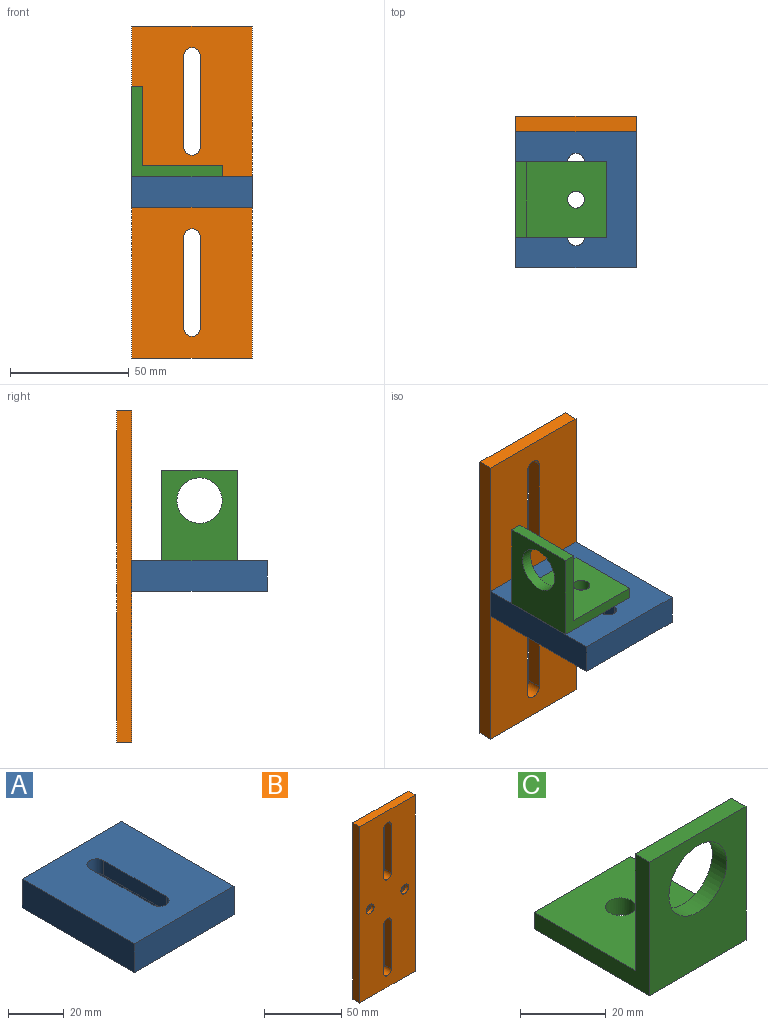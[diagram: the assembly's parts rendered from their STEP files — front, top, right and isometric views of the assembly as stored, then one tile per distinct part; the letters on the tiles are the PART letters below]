
ASSEMBLY  parts=3 mates=2
PART A: 19 faces, bbox 50.8x57.2x12.7 mm
  f0: cylinder r=3.57mm len=7.14mm, axis (0,0,-1), area 71.2mm2, adj f1,f7,f8,f14
  f1: plane 31.75x6.35mm, normal (-1,0,0), area 201.6mm2, adj f0,f2,f8,f14
  f2: cylinder r=3.57mm len=7.14mm, axis (0,0,-1), area 71.2mm2, adj f1,f7,f8,f14
  f3: plane 50.8x12.7mm, normal (0,1,0), area 604.2mm2, adj f4,f6,f8,f9,f16,f18
  f4: plane 57.15x12.7mm, normal (-1,0,0), area 725.8mm2, adj f3,f5,f8,f9
  f5: plane 50.8x12.7mm, normal (0,-1,0), area 645.2mm2, adj f4,f6,f8,f9
  f6: plane 57.15x12.7mm, normal (1,0,0), area 725.8mm2, adj f3,f5,f8,f9
  f7: plane 31.75x6.35mm, normal (1,0,0), area 201.6mm2, adj f0,f2,f8,f14
  f8: plane 57.15x50.8mm, normal (0,0,1), area 2636.6mm2, adj f0,f1,f2,f3,f4,f5,f6,f7
  f9: plane 57.15x50.8mm, normal (0,0,-1), area 2452.8mm2, adj f3,f4,f5,f6,f10,f11,f12,f13
  f10: plane 31.75x6.35mm, normal (1,0,0), area 201.6mm2, adj f9,f11,f13,f14
  f11: cylinder r=5.56mm len=11.13mm, axis (0,0,-1), area 111mm2, adj f9,f10,f12,f14
  f12: plane 31.75x6.35mm, normal (-1,0,0), area 201.6mm2, adj f9,f11,f13,f14
  f13: cylinder r=5.56mm len=11.13mm, axis (0,0,-1), area 111mm2, adj f9,f10,f12,f14
  f14: plane 42.88x11.13mm, normal (0,0,-1), area 183.8mm2, adj f0,f1,f2,f7,f10,f11,f12,f13
  f15: cone r=0mm half-angle=59deg, axis (0,1,0), area 23.9mm2, adj f16
  f16: cylinder r=2.55mm len=25.4mm, axis (0,1,0), area 407.4mm2, adj f3,f15
  f17: cone r=0mm half-angle=59deg, axis (0,1,0), area 23.9mm2, adj f18
  f18: cylinder r=2.55mm len=25.4mm, axis (0,1,0), area 407.4mm2, adj f3,f17
PART B: 18 faces, bbox 50.8x6.4x139.7 mm
  f0: plane 50.8x6.35mm, normal (0,0,1), area 322.6mm2, adj f1,f11,f12,f13
  f1: plane 139.7x6.35mm, normal (-1,0,0), area 887.1mm2, adj f0,f2,f12,f13
  f2: plane 50.8x6.35mm, normal (0,0,-1), area 322.6mm2, adj f1,f11,f12,f13
  f3: cylinder r=3.57mm len=7.14mm, axis (0,1,0), area 71.2mm2, adj f4,f9,f12,f13
  f4: plane 38.1x6.35mm, normal (-1,0,0), area 241.9mm2, adj f3,f5,f12,f13
  f5: cylinder r=3.57mm len=7.14mm, axis (0,1,0), area 71.2mm2, adj f4,f9,f12,f13
  f6: cylinder r=3.57mm len=7.14mm, axis (0,1,0), area 71.2mm2, adj f7,f10,f12,f13
  f7: plane 38.1x6.35mm, normal (-1,0,0), area 241.9mm2, adj f6,f8,f12,f13
  f8: cylinder r=3.57mm len=7.14mm, axis (0,1,0), area 71.2mm2, adj f7,f10,f12,f13
  f9: plane 38.1x6.35mm, normal (1,0,0), area 241.9mm2, adj f3,f5,f12,f13
  f10: plane 38.1x6.35mm, normal (1,0,0), area 241.9mm2, adj f6,f8,f12,f13
  f11: plane 139.7x6.35mm, normal (1,0,0), area 887.1mm2, adj f0,f2,f12,f13
  f12: plane 139.7x50.8mm, normal (0,-1,0), area 6392.8mm2, adj f0,f1,f2,f3,f4,f5,f6,f7
  f13: plane 139.7x50.8mm, normal (0,1,0), area 6187.1mm2, adj f0,f1,f2,f3,f4,f5,f6,f7
  f14: cylinder r=3.57mm len=7.14mm, axis (0,1,0), area 60.5mm2, adj f12,f15
  f15: cone r=3.57mm half-angle=41deg, axis (0,1,0), area 156.8mm2, adj f13,f14
  f16: cylinder r=3.57mm len=7.14mm, axis (0,1,0), area 60.5mm2, adj f12,f17
  f17: cone r=3.57mm half-angle=41deg, axis (0,1,0), area 156.8mm2, adj f13,f16
PART C: 10 faces, bbox 31.8x38.1x38.1 mm
  f0: plane 38.1x31.75mm, normal (0,-1,0), area 924.7mm2, adj f1,f5,f6,f7,f9
  f1: plane 38.1x31.75mm, normal (0,0,-1), area 1169.7mm2, adj f0,f2,f6,f7,f8
  f2: plane 31.75x4.76mm, normal (0,1,0), area 151.2mm2, adj f1,f3,f6,f7
  f3: plane 33.34x31.75mm, normal (0,0,1), area 1018.5mm2, adj f2,f4,f6,f7,f8
  f4: plane 33.34x31.75mm, normal (0,1,0), area 773.4mm2, adj f3,f5,f6,f7,f9
  f5: plane 31.75x4.76mm, normal (0,0,1), area 151.2mm2, adj f0,f4,f6,f7
  f6: plane 38.1x38.1mm, normal (1,0,0), area 340.2mm2, adj f0,f1,f2,f3,f4,f5
  f7: plane 38.1x38.1mm, normal (-1,0,0), area 340.2mm2, adj f0,f1,f2,f3,f4,f5
  f8: cylinder r=3.57mm len=7.14mm, axis (0,0,-1), area 106.8mm2, adj f1,f3
  f9: cylinder r=9.53mm len=19.05mm, axis (0,-1,0), area 285mm2, adj f0,f4
PLACE A t=(-6.83,-36.68,-7.83)mm
PLACE B t=(-6.83,-1.76,-1.48)mm
PLACE C rot(axis=(0,0,-1),90deg) t=(-13.18,-20.81,7.25)mm
MATE fastened C.f8 <-> A.f8  axis (0,0,-1) through (-6.83,-36.68,4.87)mm
MATE fastened A.f15 <-> B.f16  axis (0,1,0) through (9.05,-8.11,-1.48)mm
